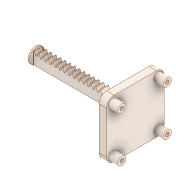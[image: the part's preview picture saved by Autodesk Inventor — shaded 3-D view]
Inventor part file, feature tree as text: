
AUTODESK INVENTOR PART (.ipt)
format: ipt  version: 2020 (Build 240168000, 168)  size: 286,208 bytes
history: mixed  units: mm
features: extrude x4, sketch x3, fillet x1, other x1, imported_body x1
ambient origin geometry x8: Origin, YZ Plane, XZ Plane, XY Plane, X Axis, Y Axis, Z Axis, Center Point
bodies: Solid1 (imported_parasolid)
feature tree (10):
  extrude  "Extrusion1"  Depth=38.0mm
  extrude  "Extrusion2"  Depth=5.0mm TaperAngle=0.0deg
  extrude  "Extrusion3"  Depth=5.0mm
  extrude  "Extrusion4"  Depth=5.0mm
  fillet  "Fillet1"  Radius=2.5mm
  sketch  "Sketch1"  dims[d0=5.0mm d1=0.0mm d2=38.0mm]
  sketch  "Sketch3"  dims[d3=38.0mm d4=5.0mm d5=0.0mm]
  sketch  "Sketch4"  dims[d6=2.5mm d7=2.5mm d8=2.5mm d9=2.5mm d10=4.0mm d11=4.0mm d12=5.0mm d13=0.0mm d14=5.5mm d15=5.5mm d16=5.5mm d17=5.5mm d18=6.0mm d19=0.0mm d20=5.0mm]
  other  "Boss-Extrude6"
  imported_body  NMx_Import_Brep_tag  [imported B-rep: ~151 faces, bbox_mm=[72.0, 38.0, 38.0]]
